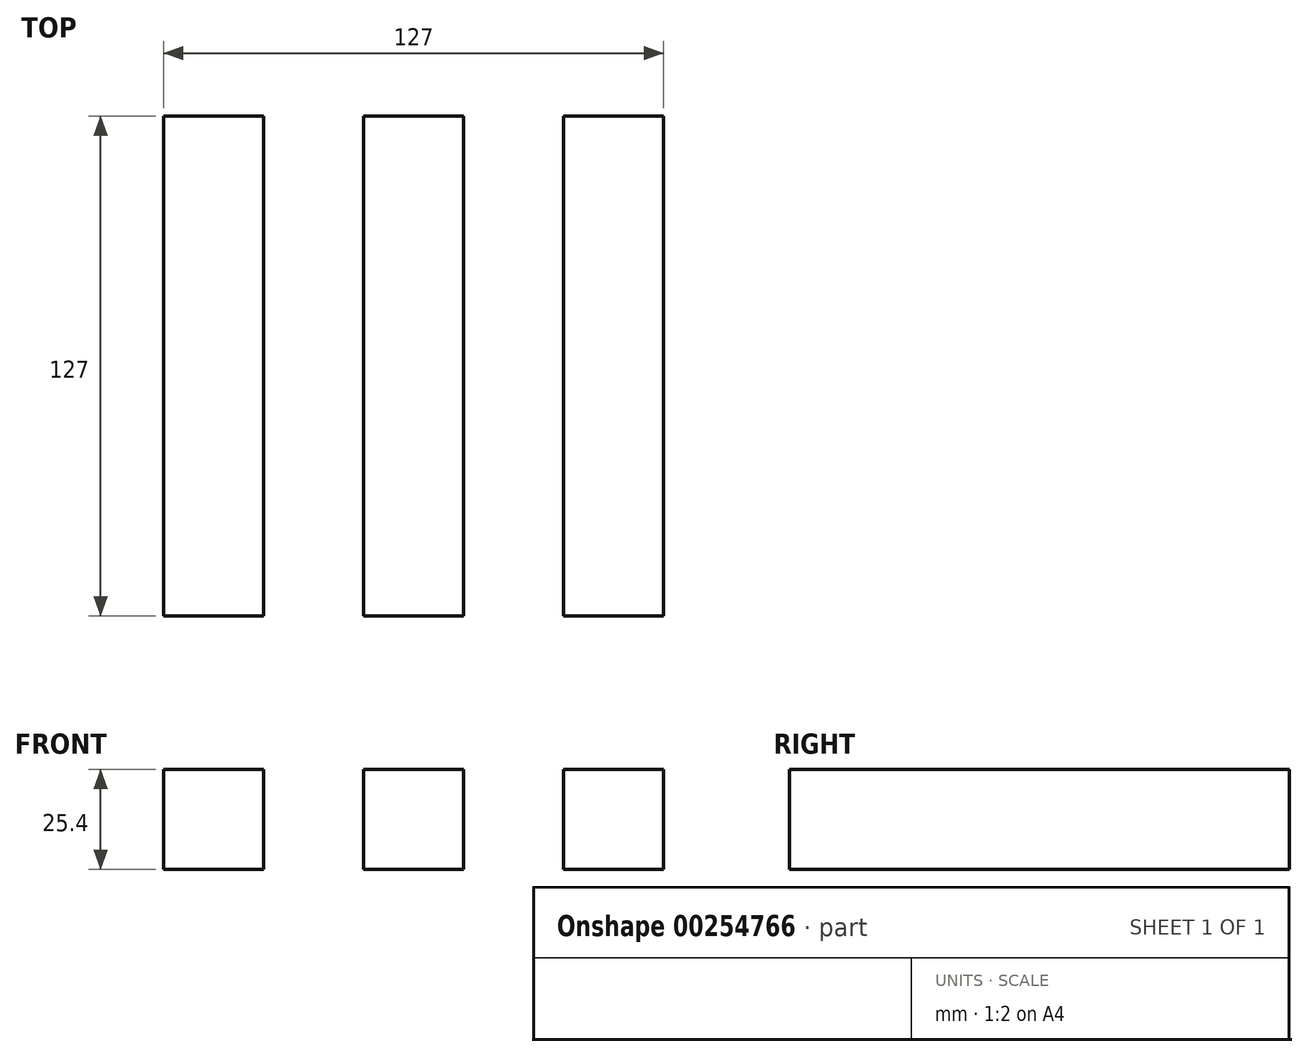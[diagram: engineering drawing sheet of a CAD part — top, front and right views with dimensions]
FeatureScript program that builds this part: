
annotation { "Feature Type Name" : "Feature", "Feature Type Description" : "" }
export const myFeature = defineFeature(function(context is Context, id is Id, definition is map)
    precondition{}
    {
        {
            var Q0;
            Q0=qCreatedBy(makeId("Front.planeOp"),FACE);
            var sketch = newSketch(context, id + "F0", { "sketchPlane" : qUnion([Q0])});
            skLineSegment(sketch, "E0.bottom", {"start": v(-12.7, 12.7) * mm, "end": v(12.7, 12.7) * mm});
            skLineSegment(sketch, "E0.top", {"start": v(-12.7, -12.7) * mm, "end": v(12.7, -12.7) * mm});
            skLineSegment(sketch, "E0.left", {"start": v(-12.7, 12.7) * mm, "end": v(-12.7, -12.7) * mm});
            skLineSegment(sketch, "E0.right", {"start": v(12.7, 12.7) * mm, "end": v(12.7, -12.7) * mm});
            skPoint(sketch, "E0.middle", {"position": v(0, 0) * mm});
            skPoint(sketch, "E1.startSnap0", {"position": v(0, 12.7) * mm});
            skLineSegment(sketch, "E2.bottom", {"start": v(63.5, 12.7) * mm, "end": v(38.1, 12.7) * mm});
            skLineSegment(sketch, "E2.top", {"start": v(63.5, -12.7) * mm, "end": v(38.1, -12.7) * mm});
            skLineSegment(sketch, "E2.left", {"start": v(63.5, 12.7) * mm, "end": v(63.5, -12.7) * mm});
            skLineSegment(sketch, "E2.right", {"start": v(38.1, 12.7) * mm, "end": v(38.1, -12.7) * mm});
            skPoint(sketch, "E2.middle", {"position": v(50.8, 0) * mm});
            skPoint(sketch, "E3.MirrorP", {"position": v(-50.8, 0) * mm});
            skLineSegment(sketch, "E4.MirrorCS", {"start": v(-63.5, 12.7) * mm, "end": v(-38.1, 12.7) * mm});
            skLineSegment(sketch, "E5.MirrorCS", {"start": v(-38.1, 12.7) * mm, "end": v(-38.1, -12.7) * mm});
            skLineSegment(sketch, "E6.MirrorCS", {"start": v(-63.5, -12.7) * mm, "end": v(-38.1, -12.7) * mm});
            skLineSegment(sketch, "E7.MirrorCS", {"start": v(-63.5, 12.7) * mm, "end": v(-63.5, -12.7) * mm});
            skSolve(sketch);
        }
        {
            var Q0;
            Q0=makeQuery(id+"F0.imprint","IMPRINT",FACE,{"disambiguationData":[TD([[makeQuery(id+"F0.imprint","IMPRINT",EDGE,{"derivedFrom":sQuery(id+"F0.wireOp",EDGE,"E4.MirrorCS")}),-1.0]])]});
            var Q1;
            Q1=makeQuery(id+"F0.imprint","IMPRINT",FACE,{"disambiguationData":[TD([[makeQuery(id+"F0.imprint","IMPRINT",EDGE,{"derivedFrom":sQuery(id+"F0.wireOp",EDGE,"E0.bottom")}),-1.0]])]});
            var Q2;
            Q2=makeQuery(id+"F0.imprint","IMPRINT",FACE,{"disambiguationData":[TD([[makeQuery(id+"F0.imprint","IMPRINT",EDGE,{"derivedFrom":sQuery(id+"F0.wireOp",EDGE,"E2.bottom")}),1.0]])]});
            extrude(context, id + "F1", {"entities" : qUnion([Q0, Q1, Q2]), "endBound" : BoundingType.SYMMETRIC, "depth" : 127 * mm});
        }
    });
